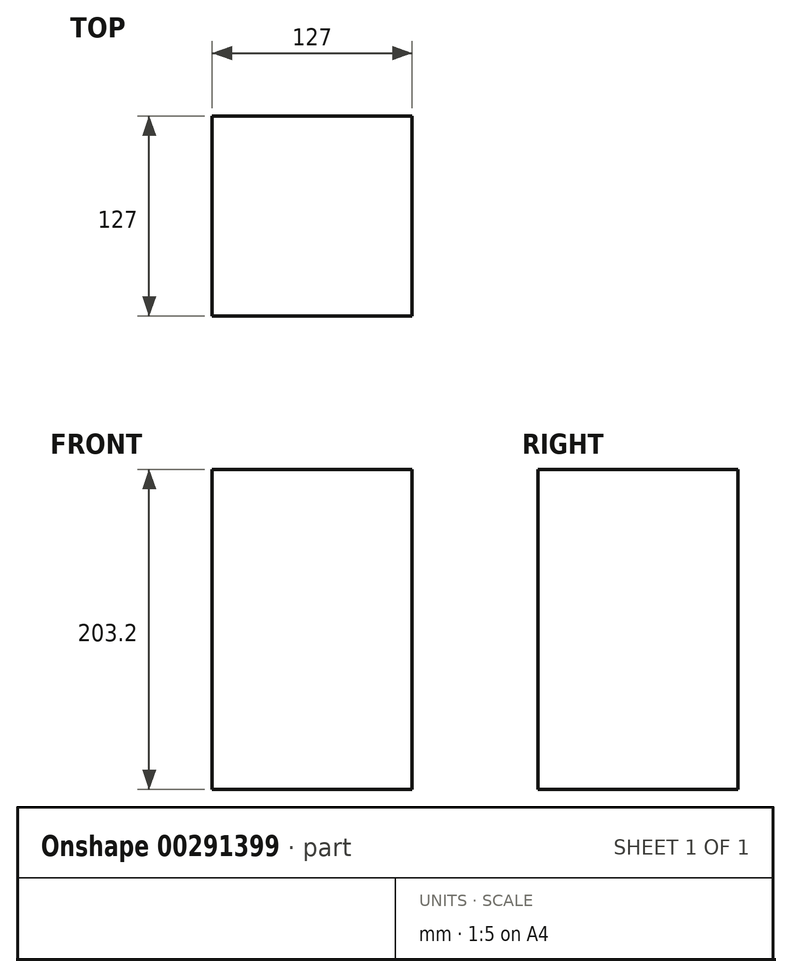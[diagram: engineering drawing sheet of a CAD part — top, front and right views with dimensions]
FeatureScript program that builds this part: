
annotation { "Feature Type Name" : "Feature", "Feature Type Description" : "" }
export const myFeature = defineFeature(function(context is Context, id is Id, definition is map)
    precondition{}
    {
        {
            var Q0;
            Q0=qCreatedBy(makeId("Front.planeOp"),FACE);
            var sketch = newSketch(context, id + "F0", { "sketchPlane" : qUnion([Q0])});
            skLineSegment(sketch, "E0.bottom", {"start": v(-63.5, 101.6) * mm, "end": v(63.5, 101.6) * mm});
            skLineSegment(sketch, "E0.top", {"start": v(-63.5, -101.6) * mm, "end": v(63.5, -101.6) * mm});
            skLineSegment(sketch, "E0.left", {"start": v(-63.5, 101.6) * mm, "end": v(-63.5, -101.6) * mm});
            skLineSegment(sketch, "E0.right", {"start": v(63.5, 101.6) * mm, "end": v(63.5, -101.6) * mm});
            skPoint(sketch, "E0.middle", {"position": v(0, 0) * mm});
            skSolve(sketch);
        }
        {
            var Q0;
            Q0 = qSketchRegion(id + "F0", true);
            extrude(context, id + "F1", {"entities" : qUnion([Q0]), "depth" : 127 * mm});
        }
    });
